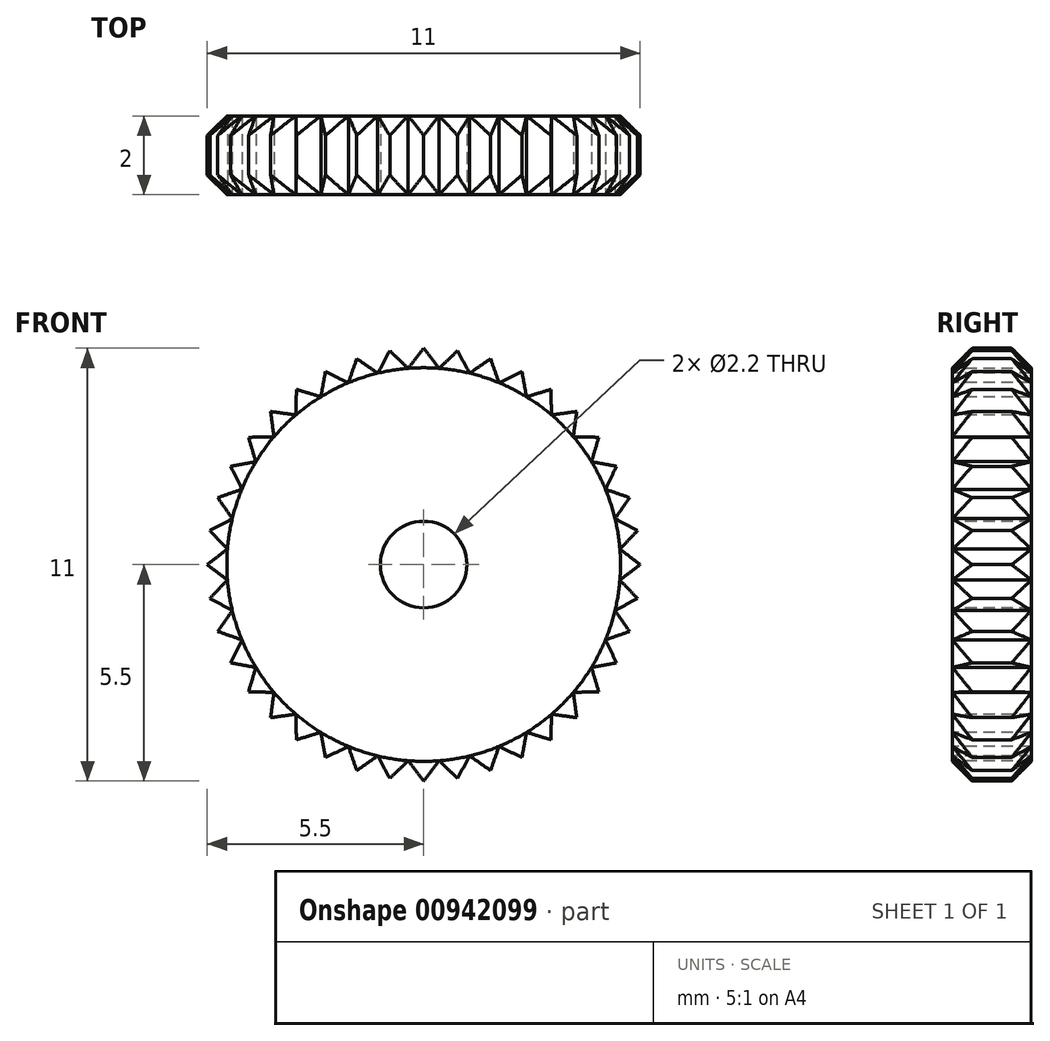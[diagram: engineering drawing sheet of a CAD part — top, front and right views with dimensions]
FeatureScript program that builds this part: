
annotation { "Feature Type Name" : "Feature", "Feature Type Description" : "" }
export const myFeature = defineFeature(function(context is Context, id is Id, definition is map)
    precondition{}
    {
        {
            var Q0;
            Q0=qCreatedBy(makeId("Front.planeOp"),FACE);
            var sketch = newSketch(context, id + "F0", { "sketchPlane" : qUnion([Q0])});
            skCircle(sketch, "E0", {"center": v(0, 0) * mm, "radius": 5 * mm});
            skLineSegment(sketch, "E1", {"start": v(-0.4, 4.98) * mm, "end": v(0, 5.5) * mm});
            skLineSegment(sketch, "E2", {"start": v(0, 5.5) * mm, "end": v(0.4, 4.98) * mm});
            skLineSegment(sketch, "E3.1.0", {"start": v(-0.86, 5.43) * mm, "end": v(-0.4, 4.98) * mm});
            skLineSegment(sketch, "E3.1.1", {"start": v(-1.17, 4.86) * mm, "end": v(-0.86, 5.43) * mm});
            skLineSegment(sketch, "E3.2.0", {"start": v(-1.7, 5.23) * mm, "end": v(-1.17, 4.86) * mm});
            skLineSegment(sketch, "E3.2.1", {"start": v(-1.91, 4.62) * mm, "end": v(-1.7, 5.23) * mm});
            skLineSegment(sketch, "E4.1.3.0", {"start": v(-2.5, 4.9) * mm, "end": v(-1.91, 4.62) * mm});
            skLineSegment(sketch, "E4.3.3.0", {"start": v(-2.61, 4.26) * mm, "end": v(-2.5, 4.9) * mm});
            skLineSegment(sketch, "E4.1.4.0", {"start": v(-3.23, 4.45) * mm, "end": v(-2.61, 4.26) * mm});
            skLineSegment(sketch, "E4.3.4.0", {"start": v(-3.25, 3.8) * mm, "end": v(-3.23, 4.45) * mm});
            skLineSegment(sketch, "E4.1.5.0", {"start": v(-3.89, 3.89) * mm, "end": v(-3.25, 3.8) * mm});
            skLineSegment(sketch, "E4.3.5.0", {"start": v(-3.8, 3.25) * mm, "end": v(-3.89, 3.89) * mm});
            skLineSegment(sketch, "E4.1.6.0", {"start": v(-4.45, 3.23) * mm, "end": v(-3.8, 3.25) * mm});
            skLineSegment(sketch, "E4.3.6.0", {"start": v(-4.26, 2.61) * mm, "end": v(-4.45, 3.23) * mm});
            skLineSegment(sketch, "E4.1.7.0", {"start": v(-4.9, 2.5) * mm, "end": v(-4.26, 2.61) * mm});
            skLineSegment(sketch, "E4.3.7.0", {"start": v(-4.62, 1.91) * mm, "end": v(-4.9, 2.5) * mm});
            skLineSegment(sketch, "E4.1.8.0", {"start": v(-5.23, 1.7) * mm, "end": v(-4.62, 1.91) * mm});
            skLineSegment(sketch, "E4.3.8.0", {"start": v(-4.86, 1.17) * mm, "end": v(-5.23, 1.7) * mm});
            skLineSegment(sketch, "E4.1.9.0", {"start": v(-5.43, 0.86) * mm, "end": v(-4.86, 1.17) * mm});
            skLineSegment(sketch, "E4.3.9.0", {"start": v(-4.98, 0.4) * mm, "end": v(-5.43, 0.86) * mm});
            skLineSegment(sketch, "E4.1.10.0", {"start": v(-5.5, 0) * mm, "end": v(-4.98, 0.4) * mm});
            skLineSegment(sketch, "E4.3.10.0", {"start": v(-4.98, -0.4) * mm, "end": v(-5.5, 0) * mm});
            skLineSegment(sketch, "E4.1.11.0", {"start": v(-5.43, -0.86) * mm, "end": v(-4.98, -0.4) * mm});
            skLineSegment(sketch, "E4.3.11.0", {"start": v(-4.86, -1.17) * mm, "end": v(-5.43, -0.86) * mm});
            skLineSegment(sketch, "E4.1.12.0", {"start": v(-5.23, -1.7) * mm, "end": v(-4.86, -1.17) * mm});
            skLineSegment(sketch, "E4.3.12.0", {"start": v(-4.62, -1.91) * mm, "end": v(-5.23, -1.7) * mm});
            skLineSegment(sketch, "E4.1.13.0", {"start": v(-4.9, -2.5) * mm, "end": v(-4.62, -1.91) * mm});
            skLineSegment(sketch, "E4.3.13.0", {"start": v(-4.26, -2.61) * mm, "end": v(-4.9, -2.5) * mm});
            skLineSegment(sketch, "E4.1.14.0", {"start": v(-4.45, -3.23) * mm, "end": v(-4.26, -2.61) * mm});
            skLineSegment(sketch, "E4.3.14.0", {"start": v(-3.8, -3.25) * mm, "end": v(-4.45, -3.23) * mm});
            skLineSegment(sketch, "E4.1.15.0", {"start": v(-3.89, -3.89) * mm, "end": v(-3.8, -3.25) * mm});
            skLineSegment(sketch, "E4.3.15.0", {"start": v(-3.25, -3.8) * mm, "end": v(-3.89, -3.89) * mm});
            skLineSegment(sketch, "E4.1.16.0", {"start": v(-3.23, -4.45) * mm, "end": v(-3.25, -3.8) * mm});
            skLineSegment(sketch, "E4.3.16.0", {"start": v(-2.61, -4.26) * mm, "end": v(-3.23, -4.45) * mm});
            skLineSegment(sketch, "E4.1.17.0", {"start": v(-2.5, -4.9) * mm, "end": v(-2.61, -4.26) * mm});
            skLineSegment(sketch, "E4.3.17.0", {"start": v(-1.91, -4.62) * mm, "end": v(-2.5, -4.9) * mm});
            skLineSegment(sketch, "E4.1.18.0", {"start": v(-1.7, -5.23) * mm, "end": v(-1.91, -4.62) * mm});
            skLineSegment(sketch, "E4.3.18.0", {"start": v(-1.17, -4.86) * mm, "end": v(-1.7, -5.23) * mm});
            skLineSegment(sketch, "E4.1.19.0", {"start": v(-0.86, -5.43) * mm, "end": v(-1.17, -4.86) * mm});
            skLineSegment(sketch, "E4.3.19.0", {"start": v(-0.4, -4.98) * mm, "end": v(-0.86, -5.43) * mm});
            skLineSegment(sketch, "E4.1.20.0", {"start": v(0, -5.5) * mm, "end": v(-0.4, -4.98) * mm});
            skLineSegment(sketch, "E4.3.20.0", {"start": v(0.4, -4.98) * mm, "end": v(0, -5.5) * mm});
            skLineSegment(sketch, "E4.1.21.0", {"start": v(0.86, -5.43) * mm, "end": v(0.4, -4.98) * mm});
            skLineSegment(sketch, "E4.3.21.0", {"start": v(1.17, -4.86) * mm, "end": v(0.86, -5.43) * mm});
            skLineSegment(sketch, "E4.1.22.0", {"start": v(1.7, -5.23) * mm, "end": v(1.17, -4.86) * mm});
            skLineSegment(sketch, "E4.3.22.0", {"start": v(1.91, -4.62) * mm, "end": v(1.7, -5.23) * mm});
            skLineSegment(sketch, "E4.1.23.0", {"start": v(2.5, -4.9) * mm, "end": v(1.91, -4.62) * mm});
            skLineSegment(sketch, "E4.3.23.0", {"start": v(2.61, -4.26) * mm, "end": v(2.5, -4.9) * mm});
            skLineSegment(sketch, "E4.1.24.0", {"start": v(3.23, -4.45) * mm, "end": v(2.61, -4.26) * mm});
            skLineSegment(sketch, "E4.3.24.0", {"start": v(3.25, -3.8) * mm, "end": v(3.23, -4.45) * mm});
            skLineSegment(sketch, "E4.1.25.0", {"start": v(3.89, -3.89) * mm, "end": v(3.25, -3.8) * mm});
            skLineSegment(sketch, "E4.3.25.0", {"start": v(3.8, -3.25) * mm, "end": v(3.89, -3.89) * mm});
            skLineSegment(sketch, "E4.1.26.0", {"start": v(4.45, -3.23) * mm, "end": v(3.8, -3.25) * mm});
            skLineSegment(sketch, "E4.3.26.0", {"start": v(4.26, -2.61) * mm, "end": v(4.45, -3.23) * mm});
            skLineSegment(sketch, "E4.1.27.0", {"start": v(4.9, -2.5) * mm, "end": v(4.26, -2.61) * mm});
            skLineSegment(sketch, "E4.3.27.0", {"start": v(4.62, -1.91) * mm, "end": v(4.9, -2.5) * mm});
            skLineSegment(sketch, "E4.1.28.0", {"start": v(5.23, -1.7) * mm, "end": v(4.62, -1.91) * mm});
            skLineSegment(sketch, "E4.3.28.0", {"start": v(4.86, -1.17) * mm, "end": v(5.23, -1.7) * mm});
            skLineSegment(sketch, "E4.1.29.0", {"start": v(5.43, -0.86) * mm, "end": v(4.86, -1.17) * mm});
            skLineSegment(sketch, "E4.3.29.0", {"start": v(4.98, -0.4) * mm, "end": v(5.43, -0.86) * mm});
            skLineSegment(sketch, "E4.1.30.0", {"start": v(5.5, 0) * mm, "end": v(4.98, -0.4) * mm});
            skLineSegment(sketch, "E4.3.30.0", {"start": v(4.98, 0.4) * mm, "end": v(5.5, 0) * mm});
            skLineSegment(sketch, "E4.1.31.0", {"start": v(5.43, 0.86) * mm, "end": v(4.98, 0.4) * mm});
            skLineSegment(sketch, "E4.3.31.0", {"start": v(4.86, 1.17) * mm, "end": v(5.43, 0.86) * mm});
            skLineSegment(sketch, "E4.1.32.0", {"start": v(5.23, 1.7) * mm, "end": v(4.86, 1.17) * mm});
            skLineSegment(sketch, "E4.3.32.0", {"start": v(4.62, 1.91) * mm, "end": v(5.23, 1.7) * mm});
            skLineSegment(sketch, "E4.1.33.0", {"start": v(4.9, 2.5) * mm, "end": v(4.62, 1.91) * mm});
            skLineSegment(sketch, "E4.3.33.0", {"start": v(4.26, 2.61) * mm, "end": v(4.9, 2.5) * mm});
            skLineSegment(sketch, "E4.1.34.0", {"start": v(4.45, 3.23) * mm, "end": v(4.26, 2.61) * mm});
            skLineSegment(sketch, "E4.3.34.0", {"start": v(3.8, 3.25) * mm, "end": v(4.45, 3.23) * mm});
            skLineSegment(sketch, "E4.1.35.0", {"start": v(3.89, 3.89) * mm, "end": v(3.8, 3.25) * mm});
            skLineSegment(sketch, "E4.3.35.0", {"start": v(3.25, 3.8) * mm, "end": v(3.89, 3.89) * mm});
            skLineSegment(sketch, "E4.1.36.0", {"start": v(3.23, 4.45) * mm, "end": v(3.25, 3.8) * mm});
            skLineSegment(sketch, "E4.3.36.0", {"start": v(2.61, 4.26) * mm, "end": v(3.23, 4.45) * mm});
            skLineSegment(sketch, "E4.1.37.0", {"start": v(2.5, 4.9) * mm, "end": v(2.61, 4.26) * mm});
            skLineSegment(sketch, "E4.3.37.0", {"start": v(1.91, 4.62) * mm, "end": v(2.5, 4.9) * mm});
            skLineSegment(sketch, "E4.1.38.0", {"start": v(1.7, 5.23) * mm, "end": v(1.91, 4.62) * mm});
            skLineSegment(sketch, "E4.3.38.0", {"start": v(1.17, 4.86) * mm, "end": v(1.7, 5.23) * mm});
            skLineSegment(sketch, "E4.1.39.0", {"start": v(0.86, 5.43) * mm, "end": v(1.17, 4.86) * mm});
            skLineSegment(sketch, "E4.3.39.0", {"start": v(0.4, 4.98) * mm, "end": v(0.86, 5.43) * mm});
            skCircle(sketch, "E5", {"center": v(0, 0) * mm, "radius": 1.1 * mm});
            skSolve(sketch);
        }
        {
            var Q0;
            Q0 = qSketchRegion(id + "F0", true);
            extrude(context, id + "F1", {"entities" : qUnion([Q0]), "oppositeDirection" : true, "depth" : 2 * mm, "offsetDistance" : 25 * mm});
        }
        {
            var Q0;
            Q0=makeQuery(id+"F1.opExtrude","CAP_FACE",FACE,{"disambiguationData":[OSD([sQuery(id+"F0.wireOp",EDGE,"E1"),sQuery(id+"F0.wireOp",EDGE,"E2"),sQuery(id+"F0.wireOp",EDGE,"E3.1.0"),sQuery(id+"F0.wireOp",EDGE,"E3.1.1"),sQuery(id+"F0.wireOp",EDGE,"E3.2.0"),sQuery(id+"F0.wireOp",EDGE,"E3.2.1"),sQuery(id+"F0.wireOp",EDGE,"E4.1.3.0"),sQuery(id+"F0.wireOp",EDGE,"E4.3.3.0"),sQuery(id+"F0.wireOp",EDGE,"E4.1.4.0"),sQuery(id+"F0.wireOp",EDGE,"E4.3.4.0"),sQuery(id+"F0.wireOp",EDGE,"E4.1.5.0"),sQuery(id+"F0.wireOp",EDGE,"E4.3.5.0"),sQuery(id+"F0.wireOp",EDGE,"E4.1.6.0"),sQuery(id+"F0.wireOp",EDGE,"E4.3.6.0"),sQuery(id+"F0.wireOp",EDGE,"E4.1.7.0"),sQuery(id+"F0.wireOp",EDGE,"E4.3.7.0"),sQuery(id+"F0.wireOp",EDGE,"E4.1.8.0"),sQuery(id+"F0.wireOp",EDGE,"E4.3.8.0"),sQuery(id+"F0.wireOp",EDGE,"E4.1.9.0"),sQuery(id+"F0.wireOp",EDGE,"E4.3.9.0"),sQuery(id+"F0.wireOp",EDGE,"E4.1.10.0"),sQuery(id+"F0.wireOp",EDGE,"E4.3.10.0"),sQuery(id+"F0.wireOp",EDGE,"E4.1.11.0"),sQuery(id+"F0.wireOp",EDGE,"E4.3.11.0"),sQuery(id+"F0.wireOp",EDGE,"E4.1.12.0"),sQuery(id+"F0.wireOp",EDGE,"E4.3.12.0"),sQuery(id+"F0.wireOp",EDGE,"E4.1.13.0"),sQuery(id+"F0.wireOp",EDGE,"E4.3.13.0"),sQuery(id+"F0.wireOp",EDGE,"E4.1.14.0"),sQuery(id+"F0.wireOp",EDGE,"E4.3.14.0"),sQuery(id+"F0.wireOp",EDGE,"E4.1.15.0"),sQuery(id+"F0.wireOp",EDGE,"E4.3.15.0"),sQuery(id+"F0.wireOp",EDGE,"E4.1.16.0"),sQuery(id+"F0.wireOp",EDGE,"E4.3.16.0"),sQuery(id+"F0.wireOp",EDGE,"E4.1.17.0"),sQuery(id+"F0.wireOp",EDGE,"E4.3.17.0"),sQuery(id+"F0.wireOp",EDGE,"E4.1.18.0"),sQuery(id+"F0.wireOp",EDGE,"E4.3.18.0"),sQuery(id+"F0.wireOp",EDGE,"E4.1.19.0"),sQuery(id+"F0.wireOp",EDGE,"E4.3.19.0"),sQuery(id+"F0.wireOp",EDGE,"E4.1.20.0"),sQuery(id+"F0.wireOp",EDGE,"E4.3.20.0"),sQuery(id+"F0.wireOp",EDGE,"E4.1.21.0"),sQuery(id+"F0.wireOp",EDGE,"E4.3.21.0"),sQuery(id+"F0.wireOp",EDGE,"E4.1.22.0"),sQuery(id+"F0.wireOp",EDGE,"E4.3.22.0"),sQuery(id+"F0.wireOp",EDGE,"E4.1.23.0"),sQuery(id+"F0.wireOp",EDGE,"E4.3.23.0"),sQuery(id+"F0.wireOp",EDGE,"E4.1.24.0"),sQuery(id+"F0.wireOp",EDGE,"E4.3.24.0"),sQuery(id+"F0.wireOp",EDGE,"E4.1.25.0"),sQuery(id+"F0.wireOp",EDGE,"E4.3.25.0"),sQuery(id+"F0.wireOp",EDGE,"E4.1.26.0"),sQuery(id+"F0.wireOp",EDGE,"E4.3.26.0"),sQuery(id+"F0.wireOp",EDGE,"E4.1.27.0"),sQuery(id+"F0.wireOp",EDGE,"E4.3.27.0"),sQuery(id+"F0.wireOp",EDGE,"E4.1.28.0"),sQuery(id+"F0.wireOp",EDGE,"E4.3.28.0"),sQuery(id+"F0.wireOp",EDGE,"E4.1.29.0"),sQuery(id+"F0.wireOp",EDGE,"E4.3.29.0"),sQuery(id+"F0.wireOp",EDGE,"E4.1.30.0"),sQuery(id+"F0.wireOp",EDGE,"E4.3.30.0"),sQuery(id+"F0.wireOp",EDGE,"E4.1.31.0"),sQuery(id+"F0.wireOp",EDGE,"E4.3.31.0"),sQuery(id+"F0.wireOp",EDGE,"E4.1.32.0"),sQuery(id+"F0.wireOp",EDGE,"E4.3.32.0"),sQuery(id+"F0.wireOp",EDGE,"E4.1.33.0"),sQuery(id+"F0.wireOp",EDGE,"E4.3.33.0"),sQuery(id+"F0.wireOp",EDGE,"E4.1.34.0"),sQuery(id+"F0.wireOp",EDGE,"E4.3.34.0"),sQuery(id+"F0.wireOp",EDGE,"E4.1.35.0"),sQuery(id+"F0.wireOp",EDGE,"E4.3.35.0"),sQuery(id+"F0.wireOp",EDGE,"E4.1.36.0"),sQuery(id+"F0.wireOp",EDGE,"E4.3.36.0"),sQuery(id+"F0.wireOp",EDGE,"E4.1.37.0"),sQuery(id+"F0.wireOp",EDGE,"E4.3.37.0"),sQuery(id+"F0.wireOp",EDGE,"E4.1.38.0"),sQuery(id+"F0.wireOp",EDGE,"E4.3.38.0"),sQuery(id+"F0.wireOp",EDGE,"E4.1.39.0"),sQuery(id+"F0.wireOp",EDGE,"E4.3.39.0")])],"isStart":false});
            var sketch = newSketch(context, id + "F2", { "sketchPlane" : qUnion([Q0])});
            skCircle(sketch, "E6", {"center": v(0, 0) * mm, "radius": 5 * mm});
            skSolve(sketch);
        }
        {
            var Q0;
            {var subQ0=sQuery(id+"F0.wireOp",EDGE,"E0");var subQ18=makeQuery(id+"F0.imprint","INTERSECT",VERTEX,{"derivedFrom":[subQ0,sQuery(id+"F0.wireOp",EDGE,"E4.3.30.0"),sQuery(id+"F0.wireOp",EDGE,"E4.1.31.0")]});Q0=makeQuery(id+"F0.imprint","IMPRINT",FACE,{"disambiguationData":[TD([[makeQuery(id+"F0.imprint","IMPRINT",EDGE,{"disambiguationData":[TD([[subQ18,-1.0]])],"derivedFrom":subQ0}),1.0]])]});}
            extrude(context, id + "F3", {"entities" : qUnion([Q0]), "operationType" : NewBodyOperationType.INTERSECT, "endBound" : BoundingType.THROUGH_ALL, "oppositeDirection" : true, "depth" : 25 * mm, "offsetDistance" : 25 * mm, "hasDraft" : true, "draftAngle" : 45 * degree});
        }
        {
            var Q0;
            {var subQ0=sQuery(id+"F2.wireOp",EDGE,"E6");var subQ17=makeQuery(id+"F2.imprint","INTERSECT",VERTEX,{"derivedFrom":[makeQuery(id+"F1.opExtrude","CAP_EDGE",EDGE,{"disambiguationData":[OSD([sQuery(id+"F0.wireOp",EDGE,"E4.3.8.0")])],"isStart":false}),makeQuery(id+"F1.opExtrude","CAP_EDGE",EDGE,{"disambiguationData":[OSD([sQuery(id+"F0.wireOp",EDGE,"E4.1.9.0")])],"isStart":false}),subQ0]});Q0=makeQuery(id+"F2.imprint","IMPRINT",FACE,{"disambiguationData":[TD([[makeQuery(id+"F2.imprint","IMPRINT",EDGE,{"disambiguationData":[TD([[subQ17,1.0]])],"derivedFrom":subQ0}),1.0]])]});}
            extrude(context, id + "F4", {"entities" : qUnion([Q0]), "operationType" : NewBodyOperationType.INTERSECT, "endBound" : BoundingType.THROUGH_ALL, "oppositeDirection" : true, "depth" : 25 * mm, "offsetDistance" : 25 * mm, "hasDraft" : true, "draftAngle" : 45 * degree});
        }
    });
